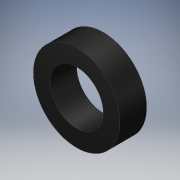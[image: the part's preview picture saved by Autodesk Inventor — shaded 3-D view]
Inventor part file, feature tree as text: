
AUTODESK INVENTOR PART (.ipt)
format: ipt  version: 2018 (Build 220112000, 112)  size: 101,376 bytes
history: native  units: mm
features: extrude x1, sketch x1
ambient origin geometry x8: Origin, YZ Plane, XZ Plane, XY Plane, X Axis, Y Axis, Z Axis, Center Point
bodies: Volumenkörper1 (feature_tree)
feature tree (2):
  extrude  "reifen_mantel"  Depth=20.0mm
  sketch  "Skizze1"  dims[d0=40.0mm d1=65.0mm d2=20.0mm d3=0.0mm]
